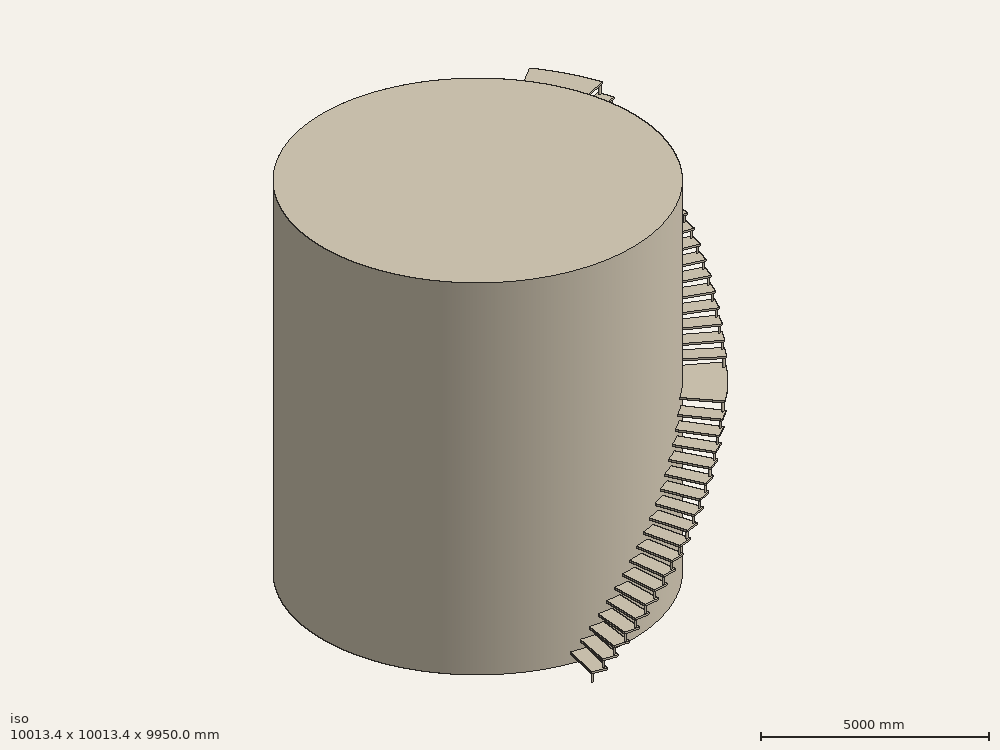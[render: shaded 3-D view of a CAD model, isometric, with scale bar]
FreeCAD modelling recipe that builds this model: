
FCSTD DOCUMENT  (FreeCAD 0.18R15419 (Git))
Label: BIG TANK
License: CreativeCommons Attribution-NonCommercial-ShareAlike
LicenseURL: http://creativecommons.org/licenses/by-nc-sa/4.0/
objects: Part::FeaturePython×8, Part::Cylinder×4, Part::MultiFuse×4, Part::Box×1
note: 17 computed .brp shape members not serialized (recipe doc carries the construction recipe); baked Part::Feature solids carry a one-line shape summary decoded from their .brp

FEATURE [Part::Box] Box  label="Cube"
  AttacherType = Attacher::AttachEngine3D
  Height = 50
  Length = 5500
  Placement = pos=(0,0,250) rot=(0,0,1;0rad)
  Width = 400
FEATURE [Part::Cylinder] Cylinder
  Angle = 360
  AttacherType = Attacher::AttachEngine3D
  Height = 250
  Placement = pos=(5450,50,0) rot=(0,0,1;0rad)
  Radius = 25
FEATURE [Part::MultiFuse] Fusion
  Shapes = -> [Box,Cylinder]
FEATURE [Part::FeaturePython] Clone  label="Fusion001"  # Draft clone (typed FeaturePython)
  AttacherType = Attacher::AttachEngine3D
  Fuse = false
  Objects = -> [Fusion]
  Placement = pos=(0,0,250) rot=(0,0,1;0.05236rad)
  Scale = (1,1,1)
FEATURE [Part::FeaturePython] Clone001  label="Fusion002"  # Draft clone (typed FeaturePython)
  AttacherType = Attacher::AttachEngine3D
  Fuse = false
  Objects = -> [Clone]
  Placement = pos=(0,0,500) rot=(0,0,1;0.10472rad)
  Scale = (1,1,1)
FEATURE [Part::FeaturePython] Clone002  label="Fusion003"  # Draft clone (typed FeaturePython)
  AttacherType = Attacher::AttachEngine3D
  Fuse = false
  Objects = -> [Clone001]
  Placement = pos=(0,0,750) rot=(0,0,1;0.15708rad)
  Scale = (1,1,1)
FEATURE [Part::FeaturePython] Clone003  label="Fusion004"  # Draft clone (typed FeaturePython)
  AttacherType = Attacher::AttachEngine3D
  Fuse = false
  Objects = -> [Clone002]
  Placement = pos=(0,0,1000) rot=(0,0,1;0.20944rad)
  Scale = (1,1,1)
FEATURE [Part::FeaturePython] Clone004  label="Fusion005"  # Draft clone (typed FeaturePython)
  AttacherType = Attacher::AttachEngine3D
  Fuse = false
  Objects = -> [Clone003]
  Placement = pos=(0,0,1250) rot=(0,0,1;0.261799rad)
  Scale = (1,1,1)
FEATURE [Part::MultiFuse] Fusion001  label="Fusion006"
  Shapes = -> [Fusion,Clone,Clone001,Clone002,Clone003,Clone004]
FEATURE [Part::FeaturePython] Clone005  label="Fusion007"  # Draft clone (typed FeaturePython)
  AttacherType = Attacher::AttachEngine3D
  Fuse = false
  Objects = -> [Fusion001]
  Placement = pos=(0,0,1500) rot=(0,0,1;0.314159rad)
  Scale = (1,1,1)
FEATURE [Part::FeaturePython] Clone006  label="Fusion008"  # Draft clone (typed FeaturePython)
  AttacherType = Attacher::AttachEngine3D
  Fuse = false
  Objects = -> [Clone005]
  Placement = pos=(0,0,3000) rot=(0,0,1;0.628319rad)
  Scale = (1,1,1)
FEATURE [Part::Cylinder] Cylinder001
  Angle = 18
  AttacherType = Attacher::AttachEngine3D
  Height = 50
  Placement = pos=(0,0,4800) rot=(0,0,1;0.942478rad)
  Radius = 5500
FEATURE [Part::Cylinder] Cylinder002
  Angle = 360
  AttacherType = Attacher::AttachEngine3D
  Height = 250
  Placement = pos=(3166.89,4435.73,4550) rot=(0,0,1;0.994838rad)
  Radius = 25
FEATURE [Part::MultiFuse] Fusion002  label="Fusion009"
  Shapes = -> [Fusion001,Clone005,Clone006,Cylinder001,Cylinder002]
FEATURE [Part::FeaturePython] Clone007  label="Fusion010"  # Draft clone (typed FeaturePython)
  AttacherType = Attacher::AttachEngine3D
  Fuse = false
  Objects = -> [Fusion002]
  Placement = pos=(0,0,4850) rot=(0,0,1;1.20428rad)
  Scale = (1,1,1)
FEATURE [Part::Cylinder] Cylinder003
  Angle = 360
  AttacherType = Attacher::AttachEngine3D
  Height = 9950
  Radius = 4500
FEATURE [Part::MultiFuse] Fusion003  label="Fusion011"
  Placement = pos=(0,0,0) rot=(0,0,1;4.39823rad)
  Shapes = -> [Fusion002,Clone007,Cylinder003]
